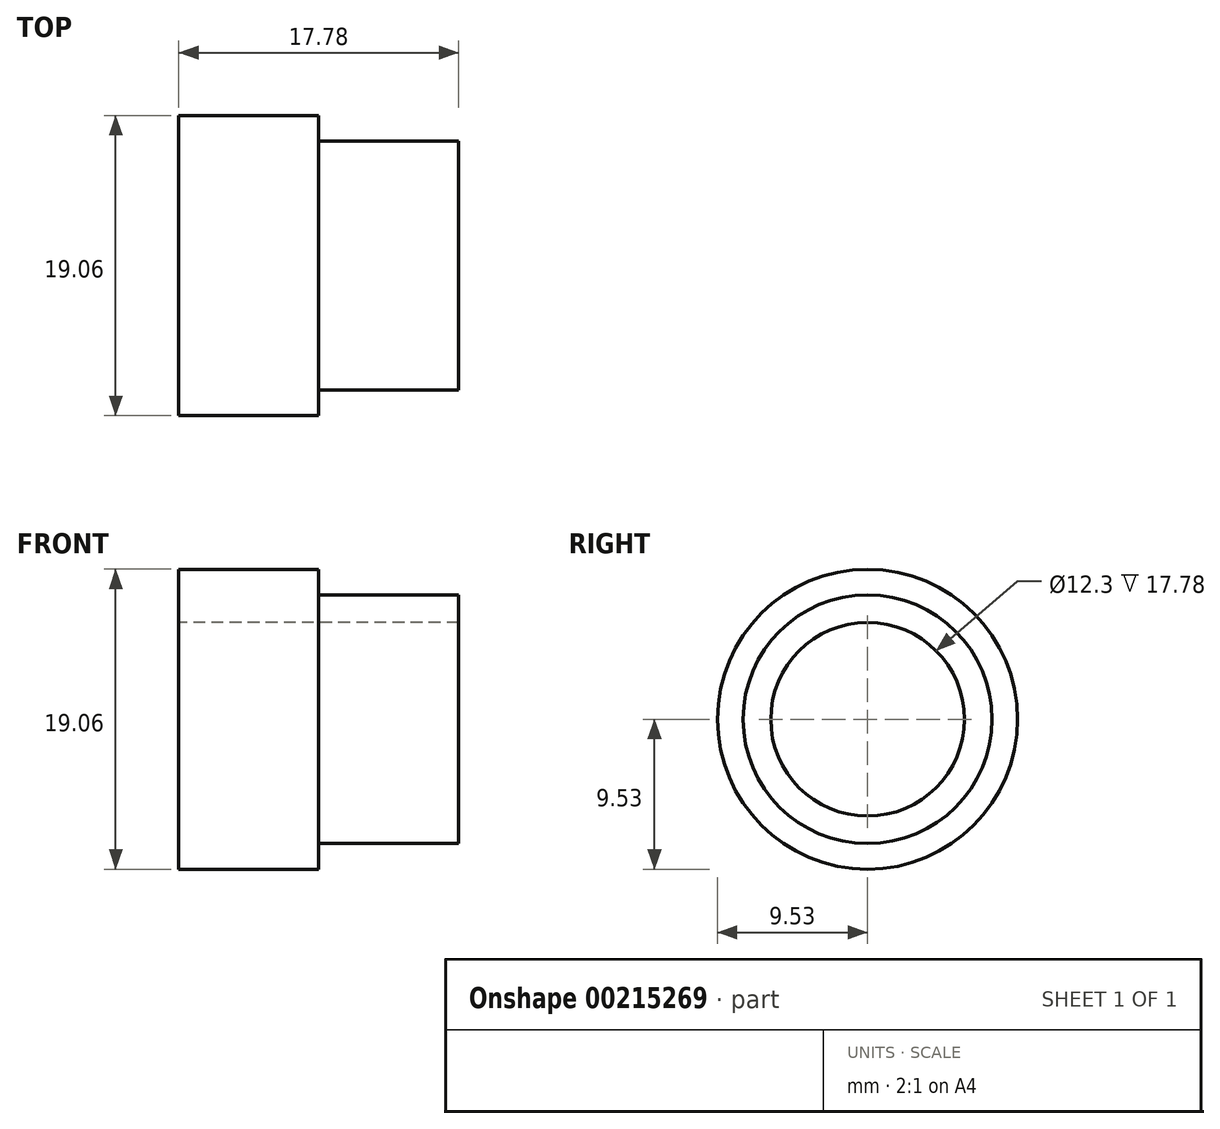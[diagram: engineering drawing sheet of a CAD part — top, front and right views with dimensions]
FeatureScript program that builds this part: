
annotation { "Feature Type Name" : "Feature", "Feature Type Description" : "" }
export const myFeature = defineFeature(function(context is Context, id is Id, definition is map)
    precondition{}
    {
        {
            var Q0;
            Q0=qCreatedBy(makeId("Top.planeOp"),FACE);
            var sketch = newSketch(context, id + "F0", { "sketchPlane" : qUnion([Q0])});
            skLineSegment(sketch, "E0", {"start": v(-87.54, 0) * mm, "end": v(100.05, 0) * mm, "construction": true});
            skLineSegment(sketch, "E1", {"start": v(-8.9, 6.15) * mm, "end": v(8.9, 6.15) * mm});
            skLineSegment(sketch, "E2", {"start": v(0, 7.9) * mm, "end": v(8.9, 7.9) * mm});
            skLineSegment(sketch, "E3", {"start": v(-8.9, 9.53) * mm, "end": v(0, 9.53) * mm});
            skLineSegment(sketch, "E4", {"start": v(-8.9, 9.53) * mm, "end": v(-8.9, 6.15) * mm});
            skLineSegment(sketch, "E5", {"start": v(0, 9.53) * mm, "end": v(0, 7.9) * mm});
            skLineSegment(sketch, "E6", {"start": v(8.9, 7.9) * mm, "end": v(8.9, 6.15) * mm});
            skSolve(sketch);
        }
        {
            var Q0;
            Q0=makeQuery(id+"F0.imprint","IMPRINT",FACE,{"disambiguationData":[TD([[makeQuery(id+"F0.imprint","IMPRINT",EDGE,{"derivedFrom":sQuery(id+"F0.wireOp",EDGE,"E1")}),1.0]])]});
            var Q1;
            Q1=sQuery(id+"F0.wireOp",EDGE,"E0");
            revolve(context, id + "F1", {"surfaceOperationType" : NewSurfaceOperationType.NEW, "entities" : qUnion([Q0]), "axis" : qUnion([Q1]), "revolveType" : RevolveType.FULL});
        }
    });
